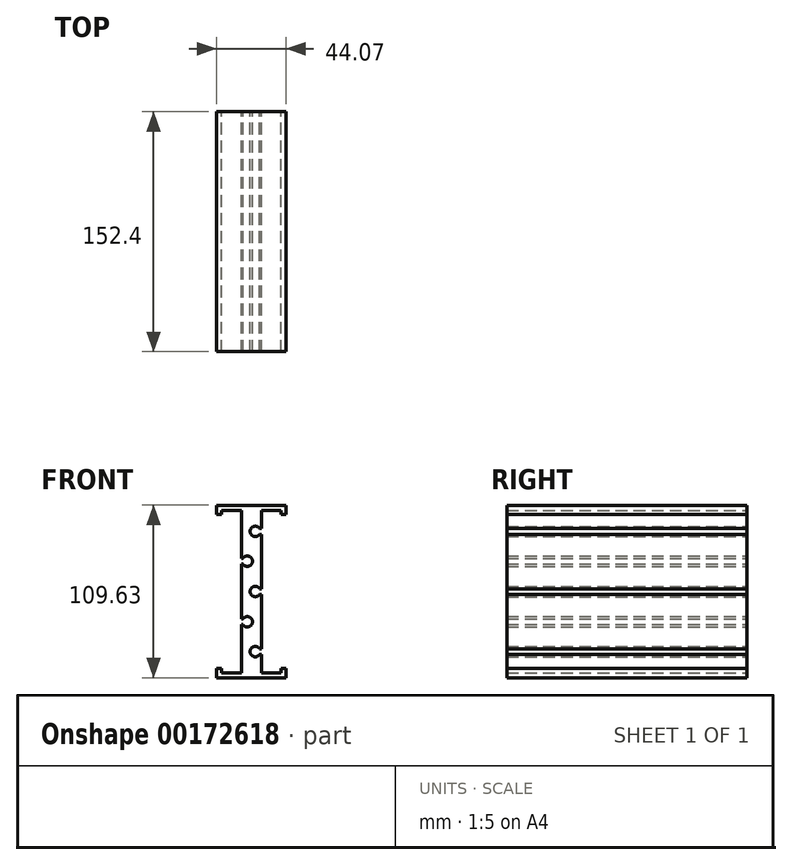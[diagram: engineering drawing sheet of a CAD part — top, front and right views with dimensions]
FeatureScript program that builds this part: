
annotation { "Feature Type Name" : "Feature", "Feature Type Description" : "" }
export const myFeature = defineFeature(function(context is Context, id is Id, definition is map)
    precondition{}
    {
        {
            var Q0;
            Q0=qCreatedBy(makeId("Front.planeOp"),FACE);
            var sketch = newSketch(context, id + "F0", { "sketchPlane" : qUnion([Q0])});
            skLineSegment(sketch, "E0", {"start": v(0, 0) * mm, "end": v(44.07, 0) * mm});
            skLineSegment(sketch, "E1", {"start": v(44.07, 0) * mm, "end": v(44.07, 5.84) * mm});
            skLineSegment(sketch, "E2", {"start": v(0, 0) * mm, "end": v(0, 5.84) * mm});
            skLineSegment(sketch, "E3", {"start": v(0, 5.84) * mm, "end": v(3.05, 5.84) * mm});
            skLineSegment(sketch, "E4", {"start": v(44.07, 5.84) * mm, "end": v(41.02, 5.84) * mm});
            skLineSegment(sketch, "E5", {"start": v(41.02, 5.84) * mm, "end": v(41.02, 3.18) * mm});
            skLineSegment(sketch, "E6", {"start": v(41.02, 3.18) * mm, "end": v(28.38, 3.18) * mm});
            skLineSegment(sketch, "E7", {"start": v(3.05, 5.84) * mm, "end": v(3.05, 3.18) * mm});
            skLineSegment(sketch, "E8", {"start": v(3.05, 3.18) * mm, "end": v(15.68, 3.18) * mm});
            skLineSegment(sketch, "E9", {"start": v(15.68, 3.17) * mm, "end": v(15.68, 33.78) * mm});
            skLineSegment(sketch, "E10", {"start": v(28.38, 3.17) * mm, "end": v(28.38, 14.86) * mm});
            skLineSegment(sketch, "E11", {"start": v(22.03, 0) * mm, "end": v(22.03, 54.81) * mm, "construction": true});
            skLineSegment(sketch, "E12", {"start": v(0, 54.81) * mm, "end": v(44.07, 54.81) * mm, "construction": true});
            skLineSegment(sketch, "E13.MirrorCS", {"start": v(0, 103.78) * mm, "end": v(3.05, 103.78) * mm});
            skLineSegment(sketch, "E14.MirrorCS", {"start": v(44.07, 103.78) * mm, "end": v(41.02, 103.78) * mm});
            skLineSegment(sketch, "E15.MirrorCS", {"start": v(41.02, 103.78) * mm, "end": v(41.02, 106.45) * mm});
            skLineSegment(sketch, "E16.MirrorCS", {"start": v(3.05, 103.78) * mm, "end": v(3.05, 106.45) * mm});
            skLineSegment(sketch, "E17.MirrorCS", {"start": v(44.07, 109.63) * mm, "end": v(44.07, 103.78) * mm});
            skLineSegment(sketch, "E18.MirrorCS", {"start": v(0, 109.63) * mm, "end": v(44.07, 109.63) * mm});
            skLineSegment(sketch, "E19.MirrorCS", {"start": v(0, 109.63) * mm, "end": v(0, 103.78) * mm});
            skLineSegment(sketch, "E20.MirrorCS", {"start": v(22.03, 109.63) * mm, "end": v(22.03, 54.81) * mm, "construction": true});
            skLineSegment(sketch, "E21.MirrorCS", {"start": v(41.02, 106.45) * mm, "end": v(28.38, 106.45) * mm});
            skLineSegment(sketch, "E22.MirrorCS", {"start": v(3.05, 106.45) * mm, "end": v(15.68, 106.45) * mm});
            skLineSegment(sketch, "E23.MirrorCS", {"start": v(15.68, 106.45) * mm, "end": v(15.68, 75.84) * mm});
            skLineSegment(sketch, "E24.MirrorCS", {"start": v(28.38, 106.45) * mm, "end": v(28.38, 94.77) * mm});
            skArc(sketch, "E25", {"start": v(27.36, 94.77) * mm, "mid": v(21.27, 92.99) * mm, "end": v(27.36, 91.21) * mm});
            skLineSegment(sketch, "E26", {"start": v(27.36, 94.77) * mm, "end": v(28.38, 94.77) * mm});
            skLineSegment(sketch, "E27", {"start": v(27.36, 91.21) * mm, "end": v(28.38, 91.21) * mm});
            skLineSegment(sketch, "E28.trimOffspring", {"start": v(28.38, 91.21) * mm, "end": v(28.38, 56.6) * mm});
            skLineSegment(sketch, "E29", {"start": v(24.57, 92.99) * mm, "end": v(28.38, 92.99) * mm, "construction": true});
            skArc(sketch, "E30", {"start": v(27.36, 56.6) * mm, "mid": v(21.27, 54.81) * mm, "end": v(27.36, 53.04) * mm});
            skLineSegment(sketch, "E31", {"start": v(27.36, 56.6) * mm, "end": v(28.38, 56.6) * mm});
            skLineSegment(sketch, "E32", {"start": v(27.36, 53.04) * mm, "end": v(28.38, 53.04) * mm});
            skPoint(sketch, "E33.orphan", {"position": v(28.38, 54.81) * mm});
            skArc(sketch, "E34", {"start": v(27.36, 18.42) * mm, "mid": v(21.27, 16.64) * mm, "end": v(27.36, 14.86) * mm});
            skLineSegment(sketch, "E35", {"start": v(27.36, 18.42) * mm, "end": v(28.38, 18.42) * mm});
            skLineSegment(sketch, "E36", {"start": v(27.36, 14.86) * mm, "end": v(28.38, 14.86) * mm});
            skLineSegment(sketch, "E37", {"start": v(24.57, 16.64) * mm, "end": v(28.38, 16.64) * mm, "construction": true});
            skLineSegment(sketch, "E38.trimOffspring", {"start": v(28.38, 18.42) * mm, "end": v(28.38, 53.04) * mm});
            skLineSegment(sketch, "E39.MirrorCS", {"start": v(16.71, 75.84) * mm, "end": v(15.68, 75.84) * mm});
            skLineSegment(sketch, "E40.MirrorCS", {"start": v(16.71, 72.29) * mm, "end": v(15.68, 72.29) * mm});
            skArc(sketch, "E41.MirrorCS", {"start": v(16.71, 75.84) * mm, "mid": v(22.8, 74.07) * mm, "end": v(16.71, 72.29) * mm});
            skLineSegment(sketch, "E42", {"start": v(19.5, 74.07) * mm, "end": v(15.68, 74.07) * mm, "construction": true});
            skLineSegment(sketch, "E43.trimOffspring", {"start": v(15.68, 72.29) * mm, "end": v(15.68, 54.81) * mm});
            skLineSegment(sketch, "E44.MirrorCS", {"start": v(16.71, 37.34) * mm, "end": v(15.68, 37.34) * mm});
            skLineSegment(sketch, "E45.MirrorCS", {"start": v(16.71, 33.78) * mm, "end": v(15.68, 33.78) * mm});
            skArc(sketch, "E46.MirrorCS", {"start": v(16.71, 33.78) * mm, "mid": v(22.8, 35.56) * mm, "end": v(16.71, 37.34) * mm});
            skLineSegment(sketch, "E47.trimOffspring", {"start": v(15.68, 37.34) * mm, "end": v(15.68, 54.81) * mm});
            skSolve(sketch);
        }
        {
            var Q0;
            Q0 = qSketchRegion(id + "F0", true);
            extrude(context, id + "F1", {"entities" : qUnion([Q0]), "depth" : 152.4 * mm});
        }
    });
